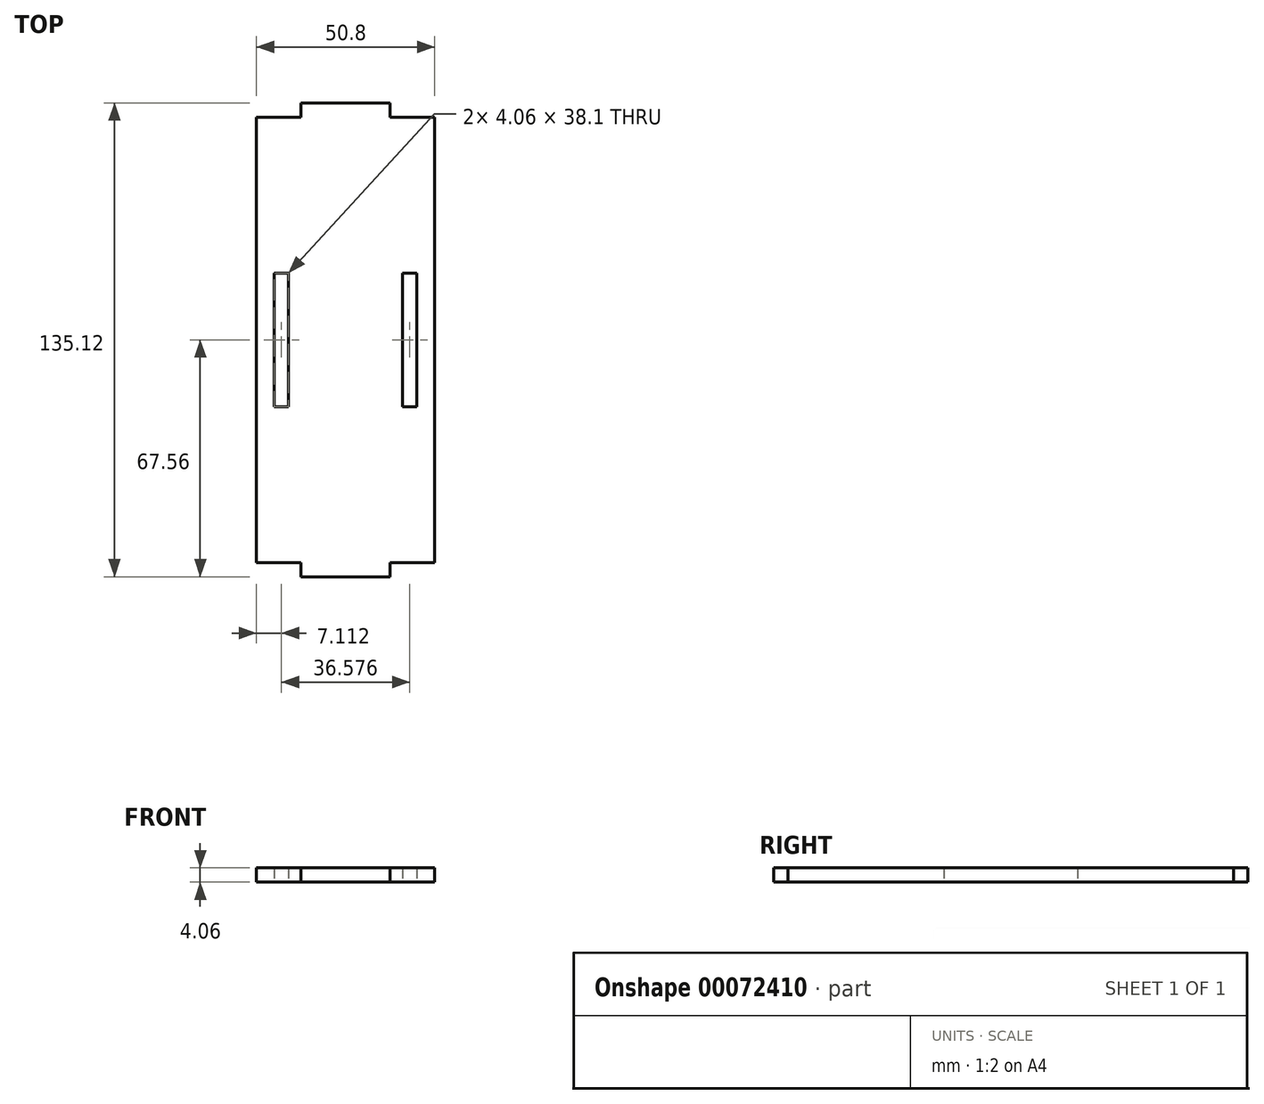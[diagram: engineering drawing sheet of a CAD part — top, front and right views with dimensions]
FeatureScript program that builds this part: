
annotation { "Feature Type Name" : "Feature", "Feature Type Description" : "" }
export const myFeature = defineFeature(function(context is Context, id is Id, definition is map)
    precondition{}
    {
        {
            var Q0;
            Q0=qCreatedBy(makeId("Top.planeOp"),FACE);
            var sketch = newSketch(context, id + "F0", { "sketchPlane" : qUnion([Q0])});
            skLineSegment(sketch, "E0.rect.bottom", {"start": v(25.4, 63.5) * mm, "end": v(-25.4, 63.5) * mm});
            skLineSegment(sketch, "E0.rect.top", {"start": v(25.4, -63.5) * mm, "end": v(-25.4, -63.5) * mm});
            skLineSegment(sketch, "E0.rect.left", {"start": v(25.4, 63.5) * mm, "end": v(25.4, -63.5) * mm});
            skLineSegment(sketch, "E0.rect.right", {"start": v(-25.4, 63.5) * mm, "end": v(-25.4, -63.5) * mm});
            skPoint(sketch, "E0.rect.middle", {"position": v(0, 0) * mm});
            skLineSegment(sketch, "E1.rect.bottom", {"start": v(12.7, -67.56) * mm, "end": v(-12.7, -67.56) * mm});
            skLineSegment(sketch, "E1.rect.top", {"start": v(12.7, -59.44) * mm, "end": v(-12.7, -59.44) * mm});
            skLineSegment(sketch, "E1.rect.left", {"start": v(12.7, -67.56) * mm, "end": v(12.7, -59.44) * mm});
            skLineSegment(sketch, "E1.rect.right", {"start": v(-12.7, -67.56) * mm, "end": v(-12.7, -59.44) * mm});
            skPoint(sketch, "E1.rect.middle", {"position": v(0, -63.5) * mm});
            skPoint(sketch, "E2.endSnap0", {"position": v(25.4, 0) * mm});
            skLineSegment(sketch, "E3", {"start": v(0, 85.33) * mm, "end": v(0, -93) * mm, "construction": true});
            skLineSegment(sketch, "E4.MirrorCS", {"start": v(12.7, 67.56) * mm, "end": v(-12.7, 67.56) * mm});
            skLineSegment(sketch, "E5.MirrorCS", {"start": v(12.7, 67.56) * mm, "end": v(12.7, 59.44) * mm});
            skLineSegment(sketch, "E6.MirrorCS", {"start": v(-12.7, 67.56) * mm, "end": v(-12.7, 59.44) * mm});
            skLineSegment(sketch, "E7.MirrorCS", {"start": v(12.7, 59.44) * mm, "end": v(-12.7, 59.44) * mm});
            skLineSegment(sketch, "E8.rect.bottom", {"start": v(20.32, 19.05) * mm, "end": v(16.26, 19.05) * mm});
            skLineSegment(sketch, "E8.rect.top", {"start": v(20.32, -19.05) * mm, "end": v(16.26, -19.05) * mm});
            skLineSegment(sketch, "E8.rect.left", {"start": v(20.32, 19.05) * mm, "end": v(20.32, -19.05) * mm});
            skLineSegment(sketch, "E8.rect.right", {"start": v(16.26, 19.05) * mm, "end": v(16.26, -19.05) * mm});
            skPoint(sketch, "E8.rect.middle", {"position": v(18.29, 0) * mm});
            skLineSegment(sketch, "E9.MirrorCS", {"start": v(-16.26, 19.05) * mm, "end": v(-16.26, -19.05) * mm});
            skLineSegment(sketch, "E10.MirrorCS", {"start": v(-20.32, 19.05) * mm, "end": v(-20.32, -19.05) * mm});
            skLineSegment(sketch, "E11.MirrorCS", {"start": v(-20.32, 19.05) * mm, "end": v(-16.26, 19.05) * mm});
            skLineSegment(sketch, "E12.MirrorCS", {"start": v(-20.32, -19.05) * mm, "end": v(-16.26, -19.05) * mm});
            skSolve(sketch);
        }
        {
            var Q0;
            {var subQ5=sQuery(id+"F0.wireOp",EDGE,"E7.MirrorCS");Q0=makeQuery(id+"F0.imprint","IMPRINT",FACE,{"disambiguationData":[TD([[makeQuery(id+"F0.imprint","IMPRINT",EDGE,{"derivedFrom":subQ5}),-1.0]])]});}
            var Q1;
            {var subQ5=sQuery(id+"F0.wireOp",EDGE,"E1.rect.bottom");Q1=makeQuery(id+"F0.imprint","IMPRINT",FACE,{"disambiguationData":[TD([[makeQuery(id+"F0.imprint","IMPRINT",EDGE,{"derivedFrom":subQ5}),-1.0]])]});}
            var Q2;
            {var subQ5=sQuery(id+"F0.wireOp",EDGE,"E4.MirrorCS");Q2=makeQuery(id+"F0.imprint","IMPRINT",FACE,{"disambiguationData":[TD([[makeQuery(id+"F0.imprint","IMPRINT",EDGE,{"derivedFrom":subQ5}),1.0]])]});}
            var Q3;
            {var subQ9=sQuery(id+"F0.wireOp",EDGE,"E0.rect.left");Q3=makeQuery(id+"F0.imprint","IMPRINT",FACE,{"disambiguationData":[TD([[makeQuery(id+"F0.imprint","IMPRINT",EDGE,{"derivedFrom":subQ9}),-1.0]])]});}
            var Q4;
            {var subQ5=sQuery(id+"F0.wireOp",EDGE,"E1.rect.top");Q4=makeQuery(id+"F0.imprint","IMPRINT",FACE,{"disambiguationData":[TD([[makeQuery(id+"F0.imprint","IMPRINT",EDGE,{"derivedFrom":subQ5}),1.0]])]});}
            extrude(context, id + "F1", {"entities" : qUnion([Q0, Q1, Q2, Q3, Q4]), "depth" : 4.06 * mm});
        }
    });
